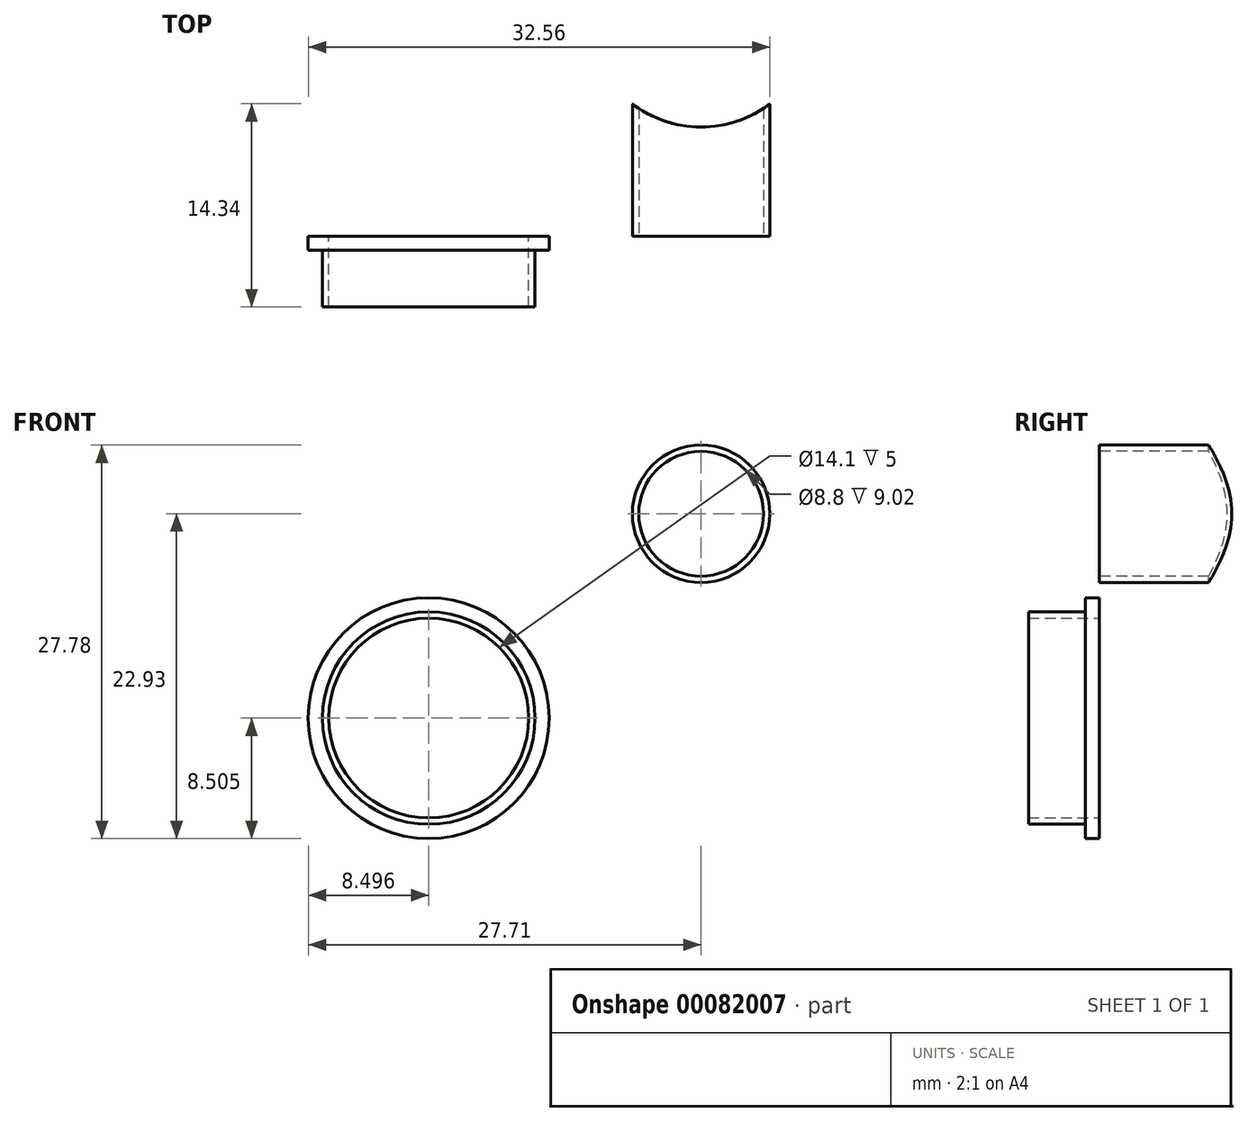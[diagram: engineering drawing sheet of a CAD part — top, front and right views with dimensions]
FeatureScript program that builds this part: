
annotation { "Feature Type Name" : "Feature", "Feature Type Description" : "" }
export const myFeature = defineFeature(function(context is Context, id is Id, definition is map)
    precondition{}
    {
        {
            var Q0;
            Q0=qCreatedBy(makeId("Front.planeOp"),FACE);
            var sketch = newSketch(context, id + "F0", { "sketchPlane" : qUnion([Q0])});
            skCircle(sketch, "E0", {"center": v(0, 0) * mm, "radius": 4.85 * mm});
            skCircle(sketch, "E1", {"center": v(0, 0) * mm, "radius": 4.4 * mm});
            skSolve(sketch);
        }
        {
            var Q0;
            Q0 = qSketchRegion(id + "F0", true);
            extrude(context, id + "F1", {"entities" : qUnion([Q0]), "oppositeDirection" : true, "depth" : 10 * mm});
        }
        {
            var Q0;
            Q0=qCreatedBy(makeId("Top.planeOp"),FACE);
            var sketch = newSketch(context, id + "F2", { "sketchPlane" : qUnion([Q0])});
            skCircle(sketch, "E2", {"center": v(0, 15.7) * mm, "radius": 8 * mm});
            skSolve(sketch);
        }
        {
            var Q0;
            Q0 = qSketchRegion(id + "F2", true);
            extrude(context, id + "F3", {"entities" : qUnion([Q0]), "operationType" : NewBodyOperationType.REMOVE, "oppositeDirection" : true, "depth" : 25 * mm, "hasSecondDirection" : true, "secondDirectionOppositeDirection" : false, "secondDirectionDepth" : 25 * mm});
        }
        {
            var Q0;
            Q0=qCreatedBy(makeId("Front.planeOp"),FACE);
            var sketch = newSketch(context, id + "F4", { "sketchPlane" : qUnion([Q0])});
            skCircle(sketch, "E3", {"center": v(-19.21, -14.43) * mm, "radius": 7.5 * mm});
            skCircle(sketch, "E4", {"center": v(-19.21, -14.43) * mm, "radius": 7.05 * mm});
            skCircle(sketch, "E5", {"center": v(-19.21, -14.43) * mm, "radius": 8.5 * mm});
            skSolve(sketch);
        }
        {
            var Q0;
            Q0=makeQuery(id+"F4.imprint","IMPRINT",FACE,{"disambiguationData":[TD([[makeQuery(id+"F4.imprint","IMPRINT",EDGE,{"derivedFrom":sQuery(id+"F4.wireOp",EDGE,"E3")}),1.0]])]});
            extrude(context, id + "F5", {"entities" : qUnion([Q0]), "depth" : 5 * mm});
        }
        {
            var Q0;
            Q0=makeQuery(id+"F4.imprint","IMPRINT",FACE,{"disambiguationData":[TD([[makeQuery(id+"F4.imprint","IMPRINT",EDGE,{"derivedFrom":sQuery(id+"F4.wireOp",EDGE,"E3")}),-1.0]])]});
            extrude(context, id + "F6", {"entities" : qUnion([Q0]), "operationType" : NewBodyOperationType.ADD, "depth" : 1 * mm});
        }
    });
